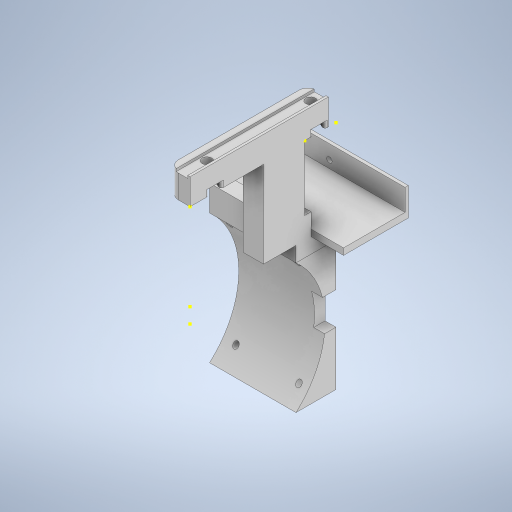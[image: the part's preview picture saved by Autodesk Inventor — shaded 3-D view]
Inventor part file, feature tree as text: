
AUTODESK INVENTOR PART (.ipt)
format: ipt  version: 2024 (Build 280153000, 153)  size: 508,928 bytes
history: native  units: in
note: dims shown in document units (in); Inventor stores cm internally (conversion verified against a paired STEP export)
features: sketch x26, extrude x18, projected_geometry x4, fillet x2, sweep x1
ambient origin geometry x8: Origin, YZ Plane, XZ Plane, XY Plane, X Axis, Y Axis, Z Axis, Center Point
bodies: Solid1 (feature_tree), Solid2 (feature_tree)
feature tree (51):
  extrude  "Extrusion1"  Depth=2.5197in
  extrude  "Extrusion2"  Depth=1.8898in
  extrude  "Extrusion3"  Depth=0.4724in TaperAngle=0.0deg
  fillet  "Fillet1"  Radius=0.0433in
  fillet  "Fillet2"  Radius=0.2126in
  extrude  "Extrusion19"  Depth=0.4724in TaperAngle=0.0deg
  extrude  "Extrusion21"  Depth=0.1181in TaperAngle=0.0deg
  sketch  "Sketch41"  dims[d17=0.1772in d18=0.0394in]
  extrude  "Extrusion22"  Depth=0.0394in
  extrude  "Extrusion25"  Depth=0.4724in
  sweep  "Sweep4"
  extrude  "Extrusion26"  Depth=0.1181in
  sketch  "Sketch60"  dims[d136=0.2756in d137=1.5748in]
  extrude  "Extrusion27"  Depth=0.3937in TaperAngle=0.0deg
  sketch  "Sketch62"  dims[d154=4.1063in d155=0.0in d164=2.3622in]
  extrude  "Extrusion28"  TaperAngle=180.0deg  [1 undecoded]
  sketch  "Sketch64"  dims[d168=2.4813in d169=0.0in d170=1.5748in d171=0.0in]
  extrude  "Extrusion29"  Depth=1.5748in
  sketch  "Sketch66"  dims[d179=0.5906in d180=0.1969in]
  sketch  "Sketch67"  dims[d181=0.5906in d182=0.8248in d183=0.0in]
  extrude  "Extrusion30"  Depth=0.2756in TaperAngle=0.0deg
  extrude  "Extrusion31"  Depth=2.3622in
  extrude  "Extrusion32"  TaperAngle=0.0deg  [1 undecoded]
  extrude  "Extrusion33"  Depth=1.5748in TaperAngle=0.0deg
  extrude  "Extrusion34"  Depth=1.5748in TaperAngle=0.0deg
  extrude  "Extrusion35"  Depth=0.1969in
  extrude  "Extrusion36"  Depth=0.8248in TaperAngle=0.0deg
  sketch  "Sketch1"  dims[d1=0.374in d2=2.5197in]
  sketch  "Sketch2"  dims[d3=0.1772in d4=1.8898in]
  sketch  "Sketch3"  dims[d6=0.1457in d7=0.4724in d8=0.0in d9=0.0433in d10=0.2126in]
  projected_geometry  "Projected Loop2"
  projected_geometry  "Projected Loop3"
  projected_geometry  "Projected Loop4"
  projected_geometry  "Projected Loop5"
  sketch  "Sketch28"  dims[d11=0.0472in d12=0.4724in d13=0.0in]
  sketch  "Sketch40"  dims[d14=0.2953in d15=0.1181in d16=0.0in]
  sketch  "Sketch42"  dims[d19=0.1575in d76=0.4724in]
  sketch  "Sketch54"  dims[d107=0.102in d108=0.748in]
  sketch  "Sketch56"  dims[d109=1.1811in d110=0.0in d130=0.1181in]
  sketch  "Sketch58"  dims[d131=0.8661in d132=0.3937in d133=0.0in]
  sketch  "Sketch59"  dims[d134=1.2008in d135=180.0deg]
  sketch  "Sketch61"  dims[d138=0.2756in d139=0.2756in d140=0.0in]
  sketch  "Sketch63"  dims[d165=1.5748in d166=0.0in d167=0.0in]
  sketch  "Sketch65"  dims[d172=0.2756in d173=1.5748in d174=0.0in]
  sketch  "Sketch68"  dims[d184=0.5906in]
  sketch  "Sketch69"  dims[d187=1.1811in]
  sketch  "Sketch70"  dims[d188=0.1181in d189=0.0in]
  sketch  "Sketch72"  dims[d190=0.1181in d191=0.0in]
  sketch  "Sketch73"  dims[d192=0.0591in]
  sketch  "Sketch74"  dims[d193=0.3937in d194=0.0in]
  sketch  "Sketch75"  dims[d195=0.0394in d196=0.1181in d197=1.4961in d198=2.2047in d199=0.1969in d200=0.1575in d201=0.0984in d202=0.1378in d203=0.1575in d204=0.0984in d205=0.0984in d206=0.1181in d207=0.0984in d208=0.1378in d209=0.1378in d210=0.0984in d211=2.8312in d212=0.0in d213=0.2756in d214=0.0787in d215=1.2008in d216=0.0in d218=0.0984in d219=0.3937in d220=0.0in d221=0.7874in d222=0.0984in d223=0.3937in d224=0.0in d42=0.0197in d43=0.0344in d44=0.0197in d45=0.0344in d46=0.0in d47=0.0in d48=0.0in d49=0.0in d50=0.0in d51=0.0in d52=0.0in d53=0.0in d55=0.0197in d56=0.0344in d57=0.0197in d58=0.0344in d60=0.0197in d61=0.0344in d62=0.0197in d63=0.0344in d72=0.0197in d73=0.0344in d74=0.0197in d75=0.0344in]
note: 2 required parameter values undecoded (feature->parameter linkage not recoverable at this tier; creation-order binding heuristic only, values carry confidence <= 0.55)
